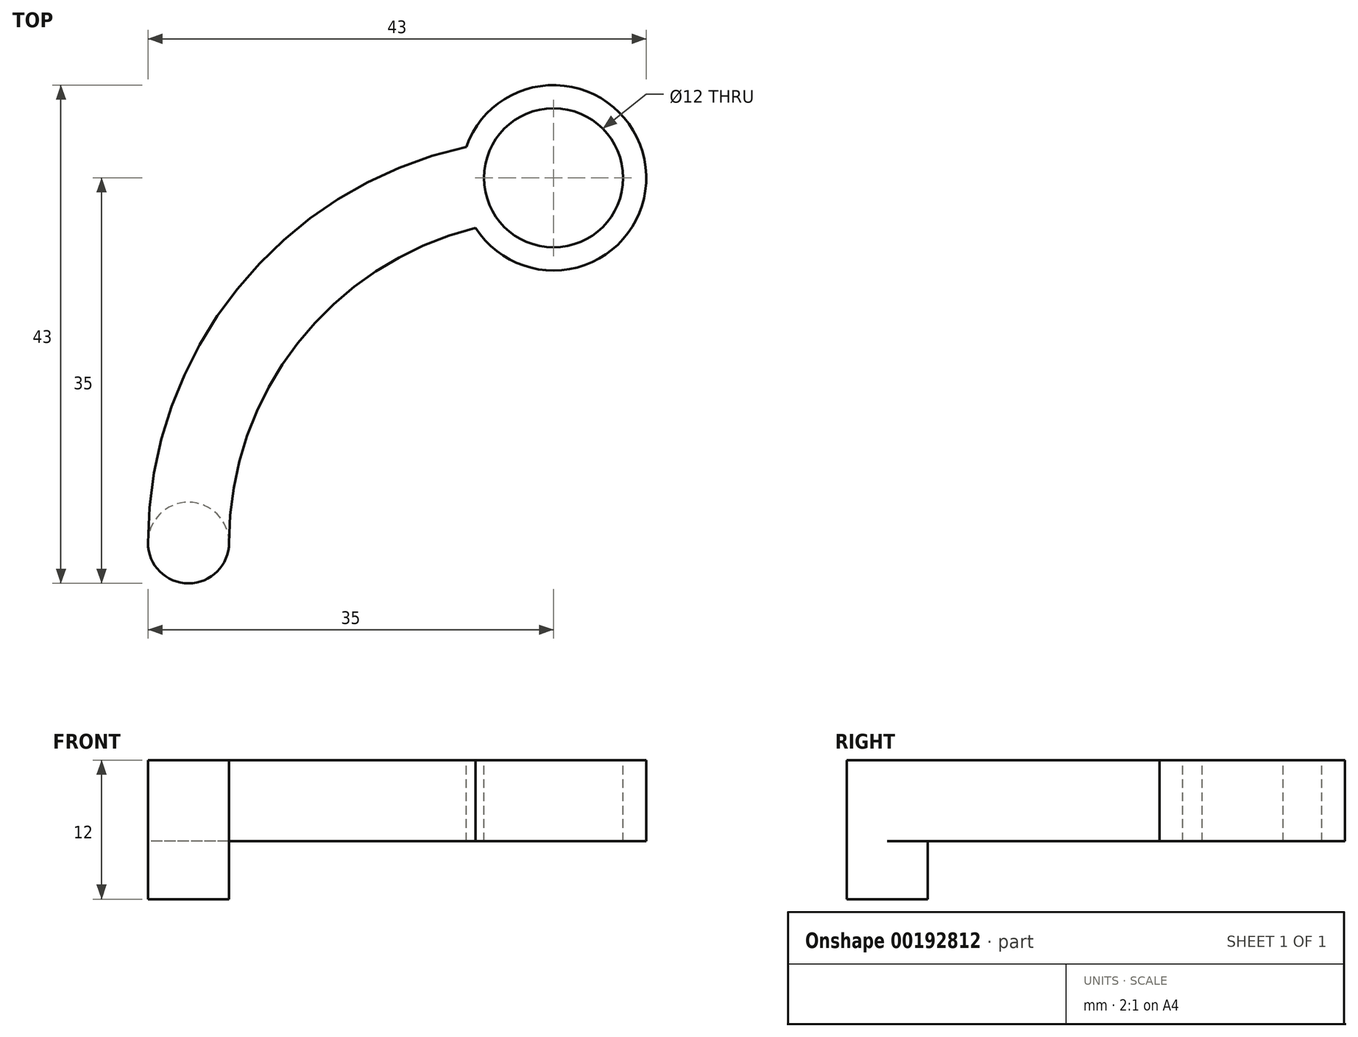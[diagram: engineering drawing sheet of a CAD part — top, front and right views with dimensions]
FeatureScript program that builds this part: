
annotation { "Feature Type Name" : "Feature", "Feature Type Description" : "" }
export const myFeature = defineFeature(function(context is Context, id is Id, definition is map)
    precondition{}
    {
        {
            var Q0;
            Q0=qCreatedBy(makeId("Top.planeOp"),FACE);
            var sketch = newSketch(context, id + "F0", { "sketchPlane" : qUnion([Q0])});
            skCircle(sketch, "E0", {"center": v(0, 0) * mm, "radius": 35 * mm});
            skSolve(sketch);
        }
        {
            var Q0;
            Q0=makeQuery(id+"F0.imprint","IMPRINT",FACE,{"disambiguationData":[TD([[makeQuery(id+"F0.imprint","IMPRINT",EDGE,{"derivedFrom":sQuery(id+"F0.wireOp",EDGE,"E0")}),1.0]])]});
            var sketch = newSketch(context, id + "F1", { "sketchPlane" : qUnion([Q0])});
            skArc(sketch, "E1", {"start": v(0, 35) * mm, "mid": v(-24.75, 24.75) * mm, "end": v(-35, 0) * mm});
            skArc(sketch, "E2", {"start": v(0, 28) * mm, "mid": v(-19.8, 19.8) * mm, "end": v(-28, 0) * mm});
            skLineSegment(sketch, "E3", {"start": v(0, 35) * mm, "end": v(0, 28) * mm});
            skLineSegment(sketch, "E4", {"start": v(-28, 0) * mm, "end": v(-35, 0) * mm});
            skSolve(sketch);
        }
        {
            var Q0;
            Q0 = qSketchRegion(id + "F0", true);
            extrude(context, id + "F2", {"entities" : qUnion([Q0]), "depth" : 7 * mm});
        }
        {
            var Q0;
            Q0 = qSketchRegion(id + "F1", true);
            extrude(context, id + "F3", {"entities" : qUnion([Q0]), "operationType" : NewBodyOperationType.INTERSECT, "endBound" : BoundingType.THROUGH_ALL, "depth" : 25 * mm});
        }
        {
            var Q0;
            Q0=makeQuery(id+"F2.opExtrude","CAP_FACE",FACE,{"disambiguationData":[OSD([sQuery(id+"F0.wireOp",EDGE,"E0")])],"isStart":false});
            var sketch = newSketch(context, id + "F4", { "sketchPlane" : qUnion([Q0])});
            skCircle(sketch, "E5", {"center": v(0, 31.5) * mm, "radius": 8 * mm});
            skSolve(sketch);
        }
        {
            var Q0;
            Q0 = qSketchRegion(id + "F4", true);
            extrude(context, id + "F5", {"entities" : qUnion([Q0]), "operationType" : NewBodyOperationType.ADD, "oppositeDirection" : true, "depth" : 7 * mm});
        }
        {
            var Q0;
            Q0=makeQuery(id+"F2.opExtrude","CAP_FACE",FACE,{"disambiguationData":[OSD([sQuery(id+"F0.wireOp",EDGE,"E0")])],"isStart":false});
            var sketch = newSketch(context, id + "F6", { "sketchPlane" : qUnion([Q0])});
            skCircle(sketch, "E6", {"center": v(-31.5, 0) * mm, "radius": 3.5 * mm});
            skSolve(sketch);
        }
        {
            var Q0;
            Q0 = qSketchRegion(id + "F6", true);
            extrude(context, id + "F7", {"entities" : qUnion([Q0]), "operationType" : NewBodyOperationType.ADD, "oppositeDirection" : true, "depth" : 12 * mm});
        }
        {
            var Q0;
            Q0=makeQuery(id+"F7.boolean.opBoolean","MERGE",FACE,{"derivedFrom":[makeQuery(id+"F5.boolean.opBoolean","MERGE",FACE,{"derivedFrom":[makeQuery(id+"F2.opExtrude","CAP_FACE",FACE,{"disambiguationData":[OSD([sQuery(id+"F0.wireOp",EDGE,"E0")])],"isStart":false}),makeQuery(id+"F5.opExtrude","CAP_FACE",FACE,{"disambiguationData":[OSD([sQuery(id+"F4.wireOp",EDGE,"E5")])],"isStart":true})]}),makeQuery(id+"F7.opExtrude","CAP_FACE",FACE,{"disambiguationData":[OSD([sQuery(id+"F6.wireOp",EDGE,"E6")])],"isStart":true})]});
            var sketch = newSketch(context, id + "F8", { "sketchPlane" : qUnion([Q0])});
            skCircle(sketch, "E7", {"center": v(0, 31.5) * mm, "radius": 6 * mm});
            skSolve(sketch);
        }
        {
            var Q0;
            Q0 = qSketchRegion(id + "F8", true);
            extrude(context, id + "F9", {"entities" : qUnion([Q0]), "operationType" : NewBodyOperationType.REMOVE, "endBound" : BoundingType.THROUGH_ALL, "oppositeDirection" : true, "depth" : 25 * mm});
        }
    });
